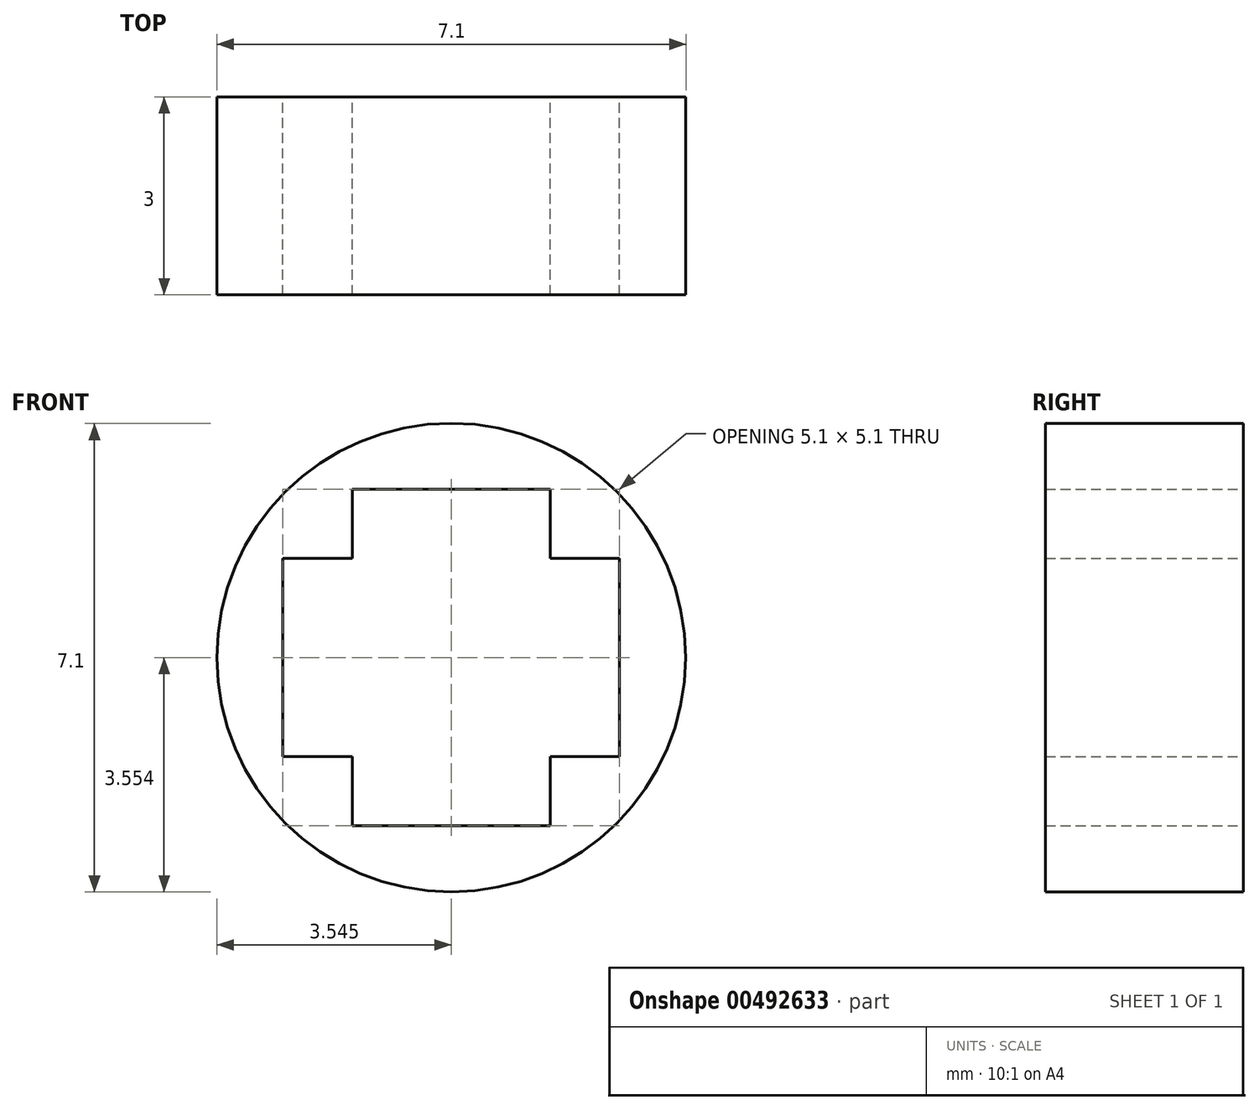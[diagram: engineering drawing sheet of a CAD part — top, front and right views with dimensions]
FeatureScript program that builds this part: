
annotation { "Feature Type Name" : "Feature", "Feature Type Description" : "" }
export const myFeature = defineFeature(function(context is Context, id is Id, definition is map)
    precondition{}
    {
        {
            var Q0;
            Q0=qCreatedBy(makeId("Front.planeOp"),FACE);
            var sketch = newSketch(context, id + "F0", { "sketchPlane" : qUnion([Q0])});
            skCircle(sketch, "E0", {"center": v(-35.18, 3.84) * mm, "radius": 3.55 * mm});
            skLineSegment(sketch, "E1.MirrorCS", {"start": v(-37.73, 5.34) * mm, "end": v(-32.63, 5.34) * mm});
            skLineSegment(sketch, "E2.MirrorCS", {"start": v(-37.73, 2.34) * mm, "end": v(-32.63, 2.34) * mm});
            skLineSegment(sketch, "E3.MirrorCS", {"start": v(-36.68, 6.4) * mm, "end": v(-36.68, 1.3) * mm});
            skLineSegment(sketch, "E4.MirrorCS", {"start": v(-33.68, 6.4) * mm, "end": v(-33.68, 1.3) * mm});
            skLineSegment(sketch, "E5", {"start": v(-37.73, 5.34) * mm, "end": v(-37.73, 2.34) * mm});
            skLineSegment(sketch, "E6", {"start": v(-32.63, 5.34) * mm, "end": v(-32.63, 2.34) * mm});
            skLineSegment(sketch, "E7", {"start": v(-36.68, 6.4) * mm, "end": v(-33.68, 6.4) * mm});
            skLineSegment(sketch, "E8", {"start": v(-36.68, 1.3) * mm, "end": v(-33.68, 1.3) * mm});
            skSolve(sketch);
        }
        {
            var Q0;
            Q0=makeQuery(id+"F0.imprint","IMPRINT",FACE,{"disambiguationData":[TD([[makeQuery(id+"F0.imprint","IMPRINT",EDGE,{"derivedFrom":sQuery(id+"F0.wireOp",EDGE,"E0")}),1.0]])]});
            extrude(context, id + "F1", {"entities" : qUnion([Q0]), "depth" : 3 * mm, "offsetDistance" : 25 * mm});
        }
    });
